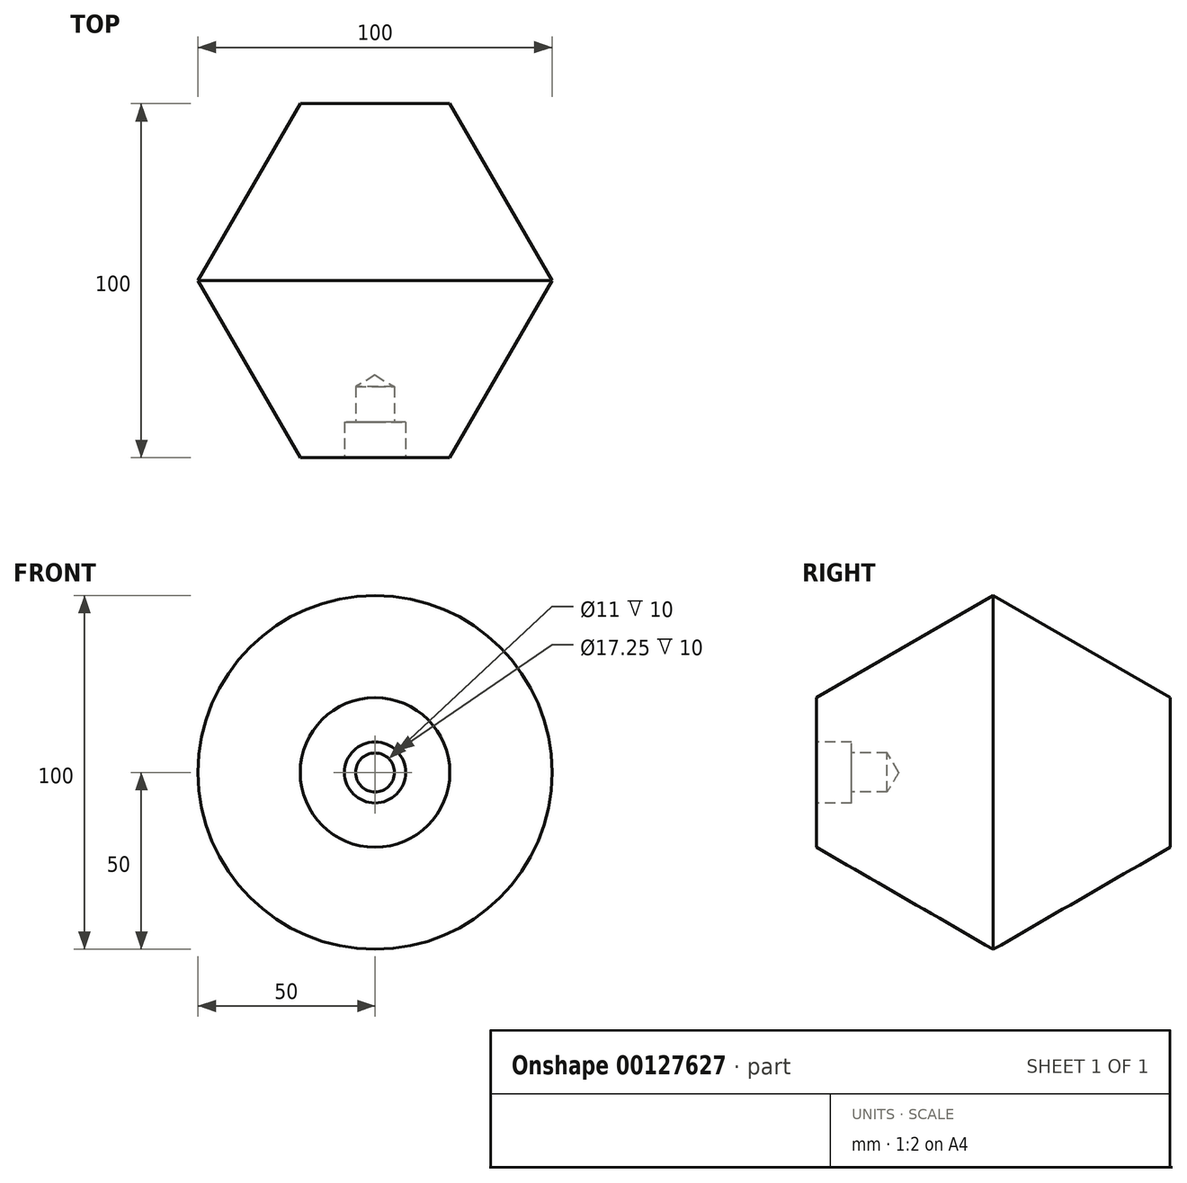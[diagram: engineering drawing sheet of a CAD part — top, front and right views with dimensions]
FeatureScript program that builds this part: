
annotation { "Feature Type Name" : "Feature", "Feature Type Description" : "" }
export const myFeature = defineFeature(function(context is Context, id is Id, definition is map)
    precondition{}
    {
        {
            var Q0;
            Q0=qCreatedBy(makeId("Front.planeOp"),FACE);
            var sketch = newSketch(context, id + "F0", { "sketchPlane" : qUnion([Q0])});
            skCircle(sketch, "E0", {"center": v(0, 0) * mm, "radius": 50 * mm});
            skSolve(sketch);
        }
        {
            var Q0;
            Q0=makeQuery(id+"F0.imprint","IMPRINT",FACE,{"disambiguationData":[TD([[makeQuery(id+"F0.imprint","IMPRINT",EDGE,{"derivedFrom":sQuery(id+"F0.wireOp",EDGE,"E0")}),1.0]])]});
            extrude(context, id + "F1", {"entities" : qUnion([Q0]), "endBound" : BoundingType.SYMMETRIC, "depth" : 100 * mm, "hasDraft" : true, "draftAngle" : 30 * degree, "draftPullDirection" : true});
        }
        {
            var Q0;
            Q0=makeQuery(id+"F1.opExtrude","CAP_FACE",FACE,{"disambiguationData":[OSD([sQuery(id+"F0.wireOp",EDGE,"E0")])],"isStart":false});
            var sketch = newSketch(context, id + "F2", { "sketchPlane" : qUnion([Q0])});
            skPoint(sketch, "E1", {"position": v(0, 0) * mm});
            skSolve(sketch);
        }
        {
            var Q0;
            Q0=sQuery(id+"F2.wireOp",VERTEX,"E1");
            var Q1;
            Q1=makeQuery(id+"F1.split0.splitOp","SPLIT",BODY,{"derivedFrom":makeQuery(id+"F1.opExtrude","SWEPT_BODY",BODY,{"disambiguationData":[OSD([sQuery(id+"F0.wireOp",EDGE,"E0")])]})});
            hole(context, id + "F3", {"style" : HoleStyle.C_BORE, "endStyle" : HoleEndStyle.BLIND, "standardTappedOrClearance" : lookupTablePath({ "standard" : "ISO", "fit" : "Normal", "size" : "M10", "type" : "Clearance" }), "standardBlindInLast" : lookupTablePath({ "fit" : "Standard", "standard" : "ISO", "size" : "M10", "type" : "Clearance" }), "holeDiameter" : 11 * mm, "cBoreDiameter" : 17.25 * mm, "cBoreDepth" : 10 * mm, "holeDepth" : 20 * mm, "locations" : qUnion([Q0]), "scope" : qUnion([Q1])});
        }
    });
